# Revit family: Workstations-Height_Adjustable-Teknion-BHKHA-Mid_Height_Kneespace_Module-R2018
name_source: partatom
category: Furniture
revit_build: Autodesk Revit 2018 (Build: 20170223_1515(x64)
units: mm (PartAtom-declared; Revit-internal decimal feet)

## family parameters
Always vertical = Yes
Cut with Voids When Loaded = No
OmniClass Number = 23.40.20.00
OmniClass Title = General Furniture and Specialties
Room Calculation Point = No
Shared = Yes
Work Plane-Based = No

## types (1)
- 9"d x 21"h
    Assembly Code = E2020200
    Description = Mid-Height Kneespace Module for Height-Adjustability, 9" Depth, 21" Height
    Manufacturer = Teknion
    Manufacturer Fax = 416.661.4586
    Model = BHKHA9__21
    Part Number = BHKHA
    Product Documentation Link = https://www.teknion.com
    Product Line = Expansion Casegoods
    Product Page URL = https://www.teknion.com
    Series = Expansion Casegoods
    Sustainability Data = https://www.teknion.com
    URL = www.teknion.com
    Unit Weight URL = http://www.teknion.com
    Warranty = http://www.teknion.com

## geometry (parser evidence)
native form markers: Sweep x3
no freeform markers — native parametric forms only
